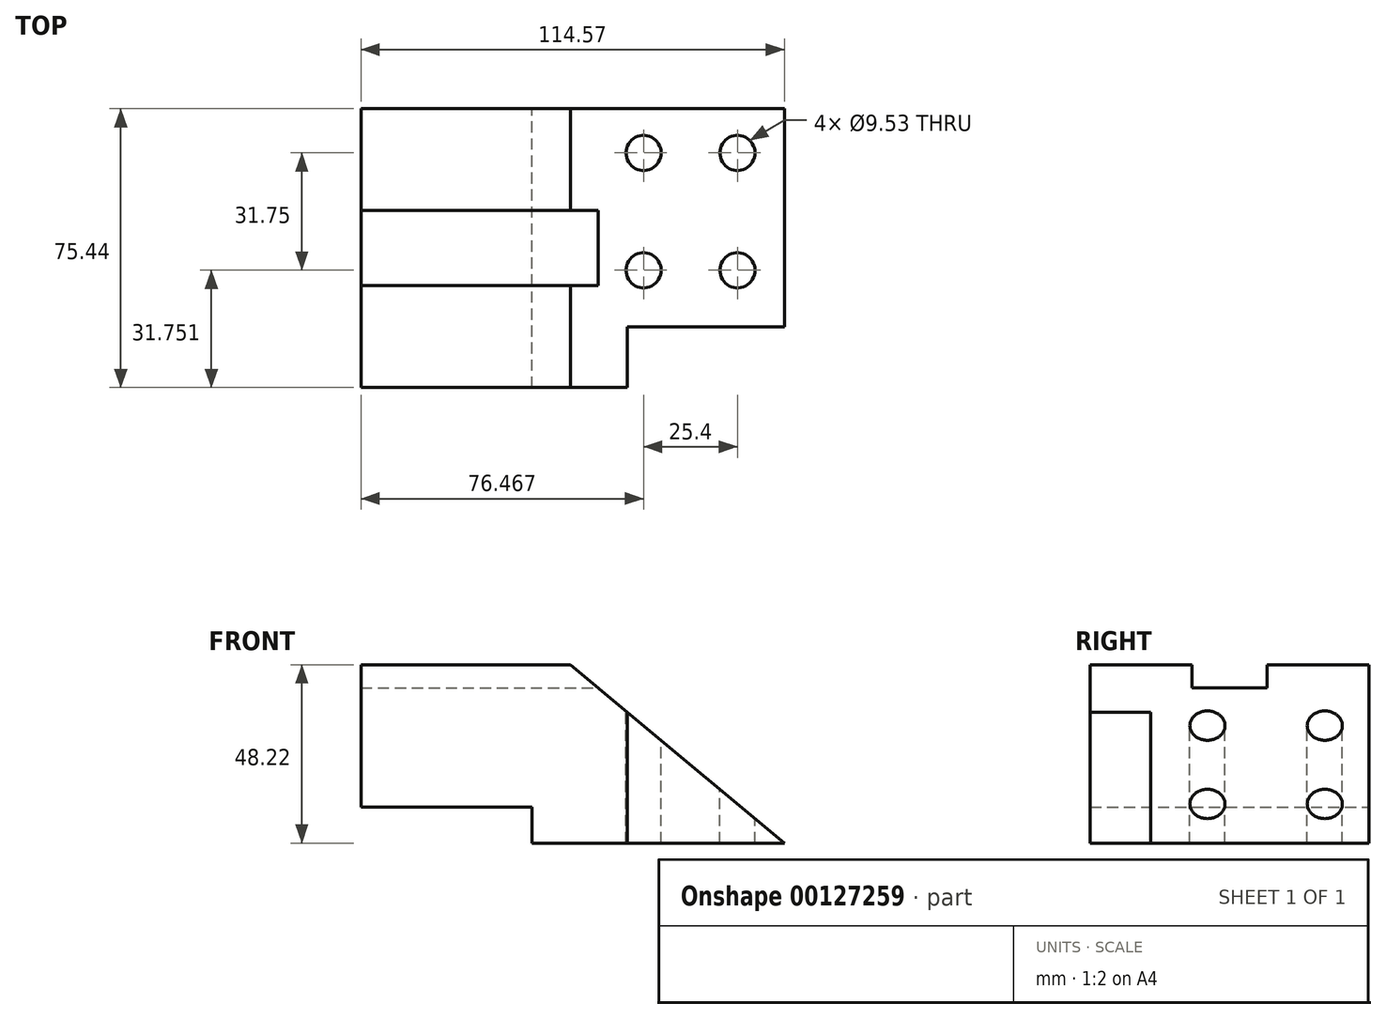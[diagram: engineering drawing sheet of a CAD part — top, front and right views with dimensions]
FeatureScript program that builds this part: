
annotation { "Feature Type Name" : "Feature", "Feature Type Description" : "" }
export const myFeature = defineFeature(function(context is Context, id is Id, definition is map)
    precondition{}
    {
        {
            var Q0;
            Q0=qCreatedBy(makeId("Front.planeOp"),FACE);
            var sketch = newSketch(context, id + "F0", { "sketchPlane" : qUnion([Q0])});
            skLineSegment(sketch, "E0", {"start": v(57.8, 0) * mm, "end": v(0, 48.22) * mm});
            skLineSegment(sketch, "E1", {"start": v(0, 48.22) * mm, "end": v(-56.76, 48.22) * mm});
            skLineSegment(sketch, "E2", {"start": v(-56.76, 48.22) * mm, "end": v(-56.76, 9.72) * mm});
            skLineSegment(sketch, "E3", {"start": v(-56.76, 9.72) * mm, "end": v(-10.51, 9.72) * mm});
            skLineSegment(sketch, "E4", {"start": v(-10.51, 9.72) * mm, "end": v(-10.51, 0) * mm});
            skLineSegment(sketch, "E5", {"start": v(-10.51, 0) * mm, "end": v(57.8, 0) * mm});
            skSolve(sketch);
        }
        {
            var Q0;
            Q0=makeQuery(id+"F0.imprint","IMPRINT",FACE,{"disambiguationData":[TD([[makeQuery(id+"F0.imprint","IMPRINT",EDGE,{"derivedFrom":sQuery(id+"F0.wireOp",EDGE,"E0")}),1.0]])]});
            extrude(context, id + "F1", {"entities" : qUnion([Q0]), "depth" : 75.44 * mm, "symmetric" : true});
        }
        {
            var Q0;
            Q0=makeQuery(id+"F1.opExtrude","SWEPT_FACE",FACE,{"disambiguationData":[OSD([sQuery(id+"F0.wireOp",EDGE,"E1")])]});
            var sketch = newSketch(context, id + "F2", { "sketchPlane" : qUnion([Q0])});
            skLineSegment(sketch, "E6.bottom", {"start": v(57.8, -37.72) * mm, "end": v(15.36, -37.72) * mm});
            skLineSegment(sketch, "E6.top", {"start": v(57.8, -21.33) * mm, "end": v(15.36, -21.33) * mm});
            skLineSegment(sketch, "E6.left", {"start": v(57.8, -37.72) * mm, "end": v(57.8, -21.33) * mm});
            skLineSegment(sketch, "E6.right", {"start": v(15.36, -37.72) * mm, "end": v(15.36, -21.33) * mm});
            skSolve(sketch);
        }
        {
            var Q0;
            Q0=makeQuery(id+"F2.imprint","IMPRINT",FACE,{"disambiguationData":[TD([[makeQuery(id+"F2.imprint","IMPRINT",EDGE,{"derivedFrom":sQuery(id+"F2.wireOp",EDGE,"E6.bottom")}),-1.0]])]});
            extrude(context, id + "F3", {"entities" : qUnion([Q0]), "operationType" : NewBodyOperationType.REMOVE, "endBound" : BoundingType.THROUGH_ALL, "oppositeDirection" : true, "depth" : 25.4 * mm});
        }
        {
            var Q0;
            Q0=qCreatedBy(makeId("Right.planeOp"),FACE);
            var sketch = newSketch(context, id + "F4", { "sketchPlane" : qUnion([Q0])});
            skLineSegment(sketch, "E7", {"start": v(0, 0) * mm, "end": v(0, 48.22) * mm, "construction": true});
            skLineSegment(sketch, "E8", {"start": v(-10.16, 42.04) * mm, "end": v(-10.16, 48.22) * mm});
            skLineSegment(sketch, "E9.0.MirrorCS", {"start": v(10.16, 42.04) * mm, "end": v(10.16, 48.22) * mm});
            skLineSegment(sketch, "E10", {"start": v(-10.16, 48.22) * mm, "end": v(10.16, 48.22) * mm});
            skLineSegment(sketch, "E11", {"start": v(-10.16, 42.04) * mm, "end": v(10.16, 42.04) * mm});
            skSolve(sketch);
        }
        {
            var Q0;
            Q0=makeQuery(id+"F4.imprint","IMPRINT",FACE,{"disambiguationData":[TD([[makeQuery(id+"F4.imprint","IMPRINT",EDGE,{"derivedFrom":sQuery(id+"F4.wireOp",EDGE,"E8")}),-1.0]])]});
            extrude(context, id + "F5", {"entities" : qUnion([Q0]), "operationType" : NewBodyOperationType.REMOVE, "endBound" : BoundingType.THROUGH_ALL, "oppositeDirection" : true, "depth" : 25.4 * mm, "hasSecondDirection" : true, "secondDirectionBound" : BoundingType.THROUGH_ALL, "secondDirectionOppositeDirection" : false, "secondDirectionDepth" : 25.4 * mm});
        }
        {
            var Q0;
            Q0=makeQuery(id+"F1.opExtrude","SWEPT_FACE",FACE,{"disambiguationData":[OSD([sQuery(id+"F0.wireOp",EDGE,"E1")])]});
            var sketch = newSketch(context, id + "F6", { "sketchPlane" : qUnion([Q0])});
            skCircle(sketch, "E12", {"center": v(19.7, -5.97) * mm, "radius": 4.76 * mm});
            skCircle(sketch, "E13", {"center": v(45.1, 25.78) * mm, "radius": 4.76 * mm});
            skCircle(sketch, "E14", {"center": v(19.7, 25.78) * mm, "radius": 4.76 * mm});
            skCircle(sketch, "E15", {"center": v(45.1, -5.97) * mm, "radius": 4.76 * mm});
            skSolve(sketch);
        }
        {
            var Q0;
            Q0=makeQuery(id+"F6.imprint","IMPRINT",FACE,{"disambiguationData":[TD([[makeQuery(id+"F6.imprint","IMPRINT",EDGE,{"derivedFrom":sQuery(id+"F6.wireOp",EDGE,"E13")}),1.0]])]});
            var Q1;
            Q1=makeQuery(id+"F6.imprint","IMPRINT",FACE,{"disambiguationData":[TD([[makeQuery(id+"F6.imprint","IMPRINT",EDGE,{"derivedFrom":sQuery(id+"F6.wireOp",EDGE,"E14")}),1.0]])]});
            var Q2;
            Q2=makeQuery(id+"F6.imprint","IMPRINT",FACE,{"disambiguationData":[TD([[makeQuery(id+"F6.imprint","IMPRINT",EDGE,{"derivedFrom":sQuery(id+"F6.wireOp",EDGE,"E12")}),1.0]])]});
            var Q3;
            Q3=makeQuery(id+"F6.imprint","IMPRINT",FACE,{"disambiguationData":[TD([[makeQuery(id+"F6.imprint","IMPRINT",EDGE,{"derivedFrom":sQuery(id+"F6.wireOp",EDGE,"E15")}),1.0]])]});
            extrude(context, id + "F7", {"entities" : qUnion([Q0, Q1, Q2, Q3]), "operationType" : NewBodyOperationType.REMOVE, "endBound" : BoundingType.THROUGH_ALL, "oppositeDirection" : true, "depth" : 25.4 * mm});
        }
    });
